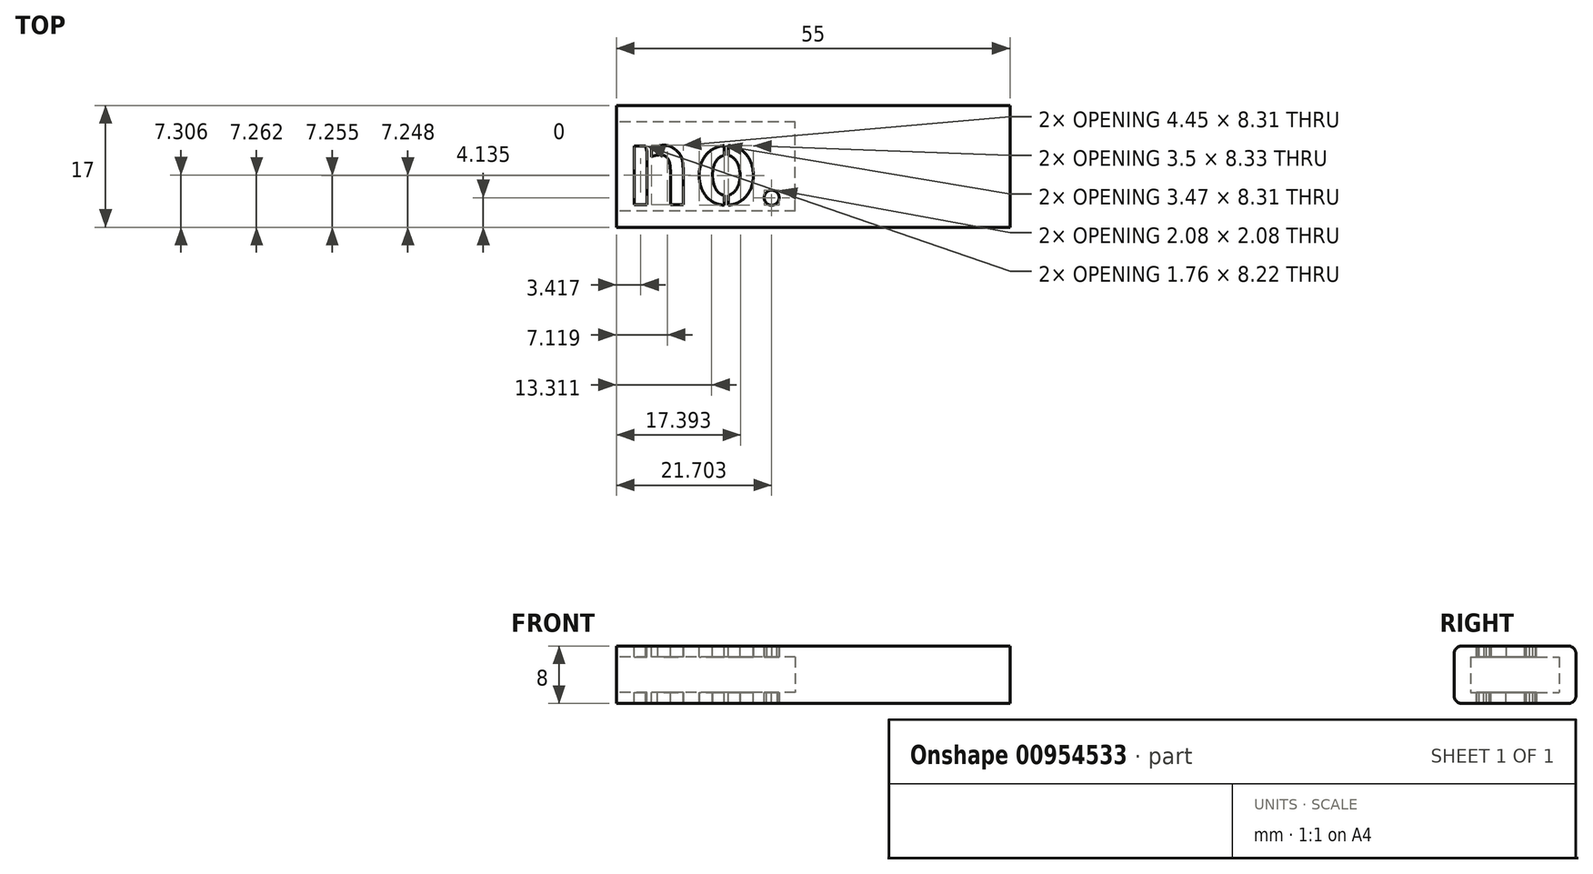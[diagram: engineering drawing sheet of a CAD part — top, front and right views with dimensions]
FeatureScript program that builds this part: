
annotation { "Feature Type Name" : "Feature", "Feature Type Description" : "" }
export const myFeature = defineFeature(function(context is Context, id is Id, definition is map)
    precondition{}
    {
        {
            var Q0;
            Q0=qCreatedBy(makeId("Front.planeOp"),FACE);
            var sketch = newSketch(context, id + "F0", { "sketchPlane" : qUnion([Q0])});
            skLineSegment(sketch, "E0.bottom", {"start": v(7.5, 4) * mm, "end": v(-7.5, 4) * mm});
            skLineSegment(sketch, "E0.top", {"start": v(7.5, -4) * mm, "end": v(-7.5, -4) * mm});
            skLineSegment(sketch, "E0.left", {"start": v(8.5, 3) * mm, "end": v(8.5, -3) * mm});
            skLineSegment(sketch, "E0.right", {"start": v(-8.5, 3) * mm, "end": v(-8.5, -3) * mm});
            skPoint(sketch, "E0.middle", {"position": v(0, 0) * mm});
            skPoint(sketch, "E1.visualSharp", {"position": v(-8.5, 4) * mm});
            skArc(sketch, "E1.filletArc", {"start": v(-7.5, 4) * mm, "mid": v(-8.2, 3.7) * mm, "end": v(-8.5, 3) * mm});
            skPoint(sketch, "E2.visualSharp", {"position": v(-8.5, -4) * mm});
            skArc(sketch, "E2.filletArc", {"start": v(-8.5, -3) * mm, "mid": v(-8.2, -3.7) * mm, "end": v(-7.5, -4) * mm});
            skPoint(sketch, "E3.visualSharp", {"position": v(8.5, -4) * mm});
            skArc(sketch, "E3.filletArc", {"start": v(7.5, -4) * mm, "mid": v(8.2, -3.7) * mm, "end": v(8.5, -3) * mm});
            skPoint(sketch, "E4.visualSharp", {"position": v(8.5, 4) * mm});
            skArc(sketch, "E4.filletArc", {"start": v(8.5, 3) * mm, "mid": v(8.2, 3.7) * mm, "end": v(7.5, 4) * mm});
            skSolve(sketch);
        }
        {
            var Q0;
            Q0 = qSketchRegion(id + "F0", true);
            extrude(context, id + "F1", {"entities" : qUnion([Q0]), "depth" : 55 * mm, "offsetDistance" : 25 * mm});
        }
        {
            var Q0;
            Q0=makeQuery(id+"F1.opExtrude","CAP_FACE",FACE,{"disambiguationData":[OSD([sQuery(id+"F0.wireOp",EDGE,"E0.bottom"),sQuery(id+"F0.wireOp",EDGE,"E0.top"),sQuery(id+"F0.wireOp",EDGE,"E0.left"),sQuery(id+"F0.wireOp",EDGE,"E0.right"),sQuery(id+"F0.wireOp",EDGE,"E1.filletArc"),sQuery(id+"F0.wireOp",EDGE,"E2.filletArc"),sQuery(id+"F0.wireOp",EDGE,"E3.filletArc"),sQuery(id+"F0.wireOp",EDGE,"E4.filletArc")])],"isStart":false});
            var sketch = newSketch(context, id + "F2", { "sketchPlane" : qUnion([Q0])});
            skLineSegment(sketch, "E5.bottom", {"start": v(6.2, 2.5) * mm, "end": v(-6.2, 2.5) * mm});
            skLineSegment(sketch, "E5.top", {"start": v(6.2, -2.5) * mm, "end": v(-6.2, -2.5) * mm});
            skLineSegment(sketch, "E5.left", {"start": v(6.2, 2.5) * mm, "end": v(6.2, -2.5) * mm});
            skLineSegment(sketch, "E5.right", {"start": v(-6.2, 2.5) * mm, "end": v(-6.2, -2.5) * mm});
            skPoint(sketch, "E5.middle", {"position": v(0, 0) * mm});
            skSolve(sketch);
        }
        {
            var Q0;
            Q0 = qSketchRegion(id + "F2", true);
            extrude(context, id + "F3", {"entities" : qUnion([Q0]), "operationType" : NewBodyOperationType.REMOVE, "oppositeDirection" : true, "depth" : 25 * mm, "offsetDistance" : 25 * mm});
        }
        {
            var Q0;
            Q0=makeQuery(id+"F1.opExtrude","SWEPT_BODY",BODY,{"disambiguationData":[OSD([sQuery(id+"F0.wireOp",EDGE,"E0.bottom"),sQuery(id+"F0.wireOp",EDGE,"E0.top"),sQuery(id+"F0.wireOp",EDGE,"E0.left"),sQuery(id+"F0.wireOp",EDGE,"E0.right"),sQuery(id+"F0.wireOp",EDGE,"E1.filletArc"),sQuery(id+"F0.wireOp",EDGE,"E2.filletArc"),sQuery(id+"F0.wireOp",EDGE,"E3.filletArc"),sQuery(id+"F0.wireOp",EDGE,"E4.filletArc")])]});
            var Q1;
            Q1=makeQuery(id+"F1.opExtrude","CAP_EDGE",EDGE,{"disambiguationData":[OSD([sQuery(id+"F0.wireOp",EDGE,"E0.left")])],"isStart":true});
            transform(context, id + "F4", {"entities" : qUnion([Q0]), "transformType" : TransformType.ROTATION, "transformAxis" : qUnion([Q1]), "angle" : 90 * degree, "makeCopy" : false});
        }
        {
            var Q0;
            Q0=makeQuery(id+"F1.opExtrude","SWEPT_FACE",FACE,{"disambiguationData":[OSD([sQuery(id+"F0.wireOp",EDGE,"E0.bottom")])]});
            var sketch = newSketch(context, id + "F5", { "sketchPlane" : qUnion([Q0])});
            skSolve(sketch);
        }
        {
            var Q0;
            {var subQ0=sQuery(id+"F0.wireOp",EDGE,"E0.bottom");Q0=makeQuery(id+"F5.imprint","IMPRINT",FACE,{"disambiguationData":[TD([[makeQuery(id+"F5.imprint","IMPRINT",EDGE,{"derivedFrom":makeQuery(id+"F1.opExtrude","CAP_EDGE",EDGE,{"disambiguationData":[OSD([subQ0])],"isStart":true})}),1.0]])]});}
            var sketch = newSketch(context, id + "F6", { "sketchPlane" : qUnion([Q0])});
            skSolve(sketch);
        }
        {
            var Q0;
            {var subQ0=sQuery(id+"F0.wireOp",EDGE,"E0.bottom");Q0=makeQuery(id+"F6.imprint","IMPRINT",FACE,{"disambiguationData":[TD([[makeQuery(id+"F6.imprint","IMPRINT",EDGE,{"derivedFrom":makeQuery(id+"F5.imprint","IMPRINT",EDGE,{"derivedFrom":makeQuery(id+"F1.opExtrude","CAP_EDGE",EDGE,{"disambiguationData":[OSD([subQ0])],"isStart":true})})}),1.0]])]});}
            var sketch = newSketch(context, id + "F7", { "sketchPlane" : qUnion([Q0])});
            skText(sketch, "E6", { "text": "no.", "fontName": "AllertaStencil-Regular.ttf"});
            const initialGuessF7  = {"E6": [-0.04522, 0.00315, 1, 0, 0.01075]};
            skSetInitialGuess(sketch, initialGuessF7);
            skSolve(sketch);
        }
        {
            var Q0;
            Q0 = qSketchRegion(id + "F7", true);
            extrude(context, id + "F8", {"entities" : qUnion([Q0]), "operationType" : NewBodyOperationType.REMOVE, "oppositeDirection" : true, "depth" : 10 * mm, "offsetDistance" : 25 * mm});
        }
    });
